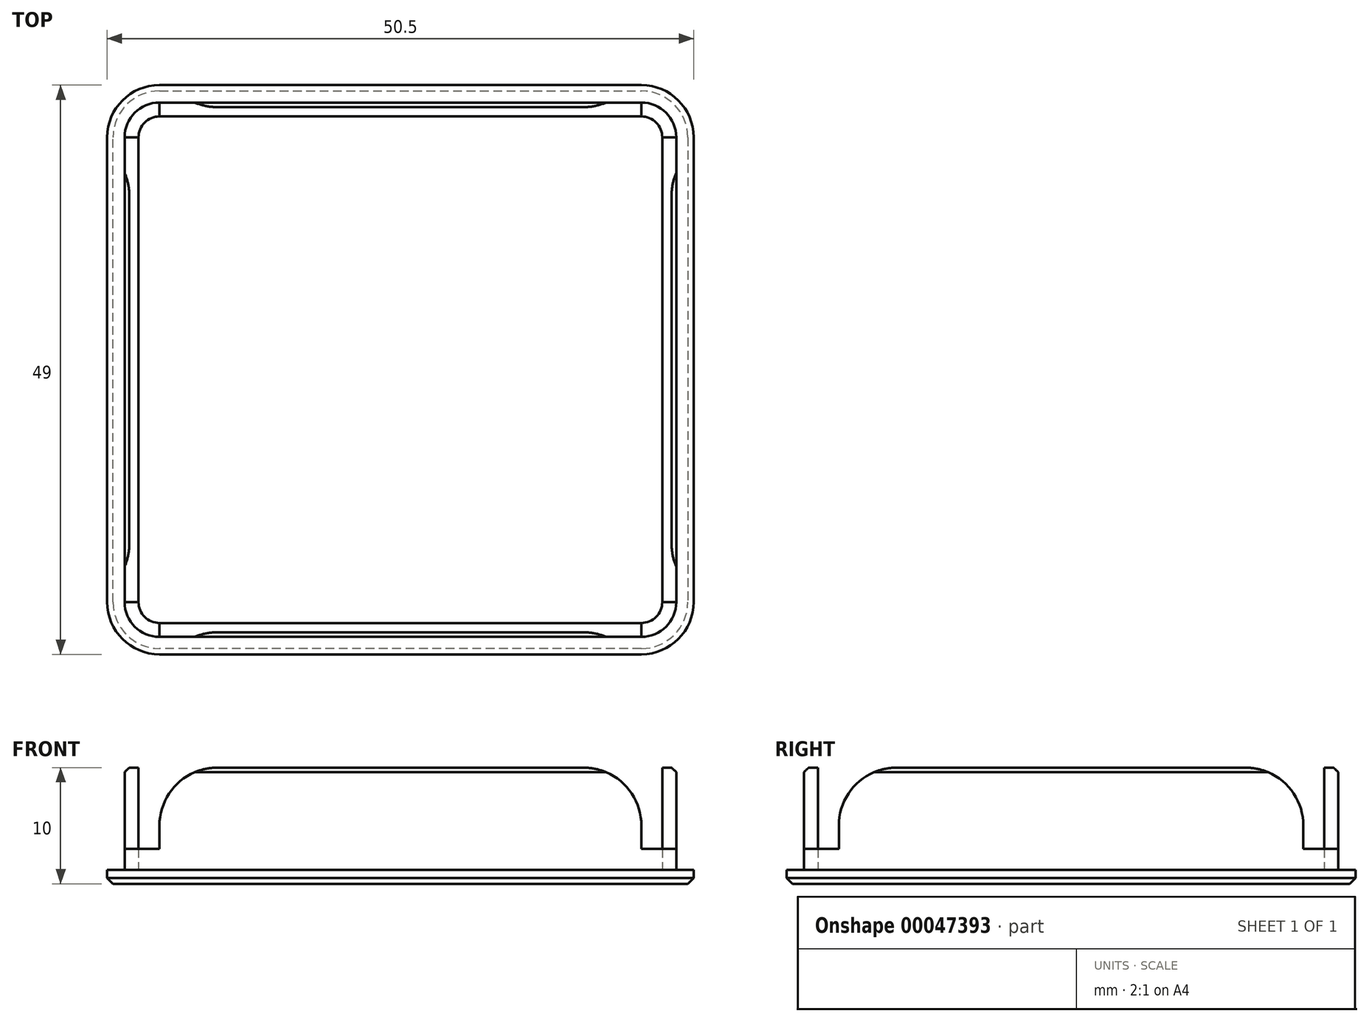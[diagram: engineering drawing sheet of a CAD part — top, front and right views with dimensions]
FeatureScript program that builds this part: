
annotation { "Feature Type Name" : "Feature", "Feature Type Description" : "" }
export const myFeature = defineFeature(function(context is Context, id is Id, definition is map)
    precondition{}
    {
        {
            var Q0;
            Q0=qCreatedBy(makeId("Top.planeOp"),FACE);
            var sketch = newSketch(context, id + "F0", { "sketchPlane" : qUnion([Q0])});
            skLineSegment(sketch, "E0.bottom", {"start": v(3, 0) * mm, "end": v(44.5, 0) * mm});
            skLineSegment(sketch, "E0.top", {"start": v(3, 46) * mm, "end": v(44.5, 46) * mm});
            skLineSegment(sketch, "E0.left", {"start": v(0, 3) * mm, "end": v(0, 43) * mm});
            skLineSegment(sketch, "E0.right", {"start": v(47.5, 3) * mm, "end": v(47.5, 43) * mm});
            skLineSegment(sketch, "E1.0", {"start": v(3, 47.5) * mm, "end": v(44.5, 47.5) * mm});
            skLineSegment(sketch, "E1.1", {"start": v(-1.5, 3) * mm, "end": v(-1.5, 43) * mm});
            skLineSegment(sketch, "E1.2", {"start": v(3, -1.5) * mm, "end": v(44.5, -1.5) * mm});
            skLineSegment(sketch, "E1.3", {"start": v(49, 3) * mm, "end": v(49, 43) * mm});
            skPoint(sketch, "E2.visualSharp", {"position": v(-1.5, 47.5) * mm});
            skArc(sketch, "E2.filletArc", {"start": v(3, 47.5) * mm, "mid": v(-0.18, 46.18) * mm, "end": v(-1.5, 43) * mm});
            skPoint(sketch, "E3.visualSharp", {"position": v(49, 47.5) * mm});
            skArc(sketch, "E3.filletArc", {"start": v(49, 43) * mm, "mid": v(47.68, 46.18) * mm, "end": v(44.5, 47.5) * mm});
            skPoint(sketch, "E4.visualSharp", {"position": v(49, -1.5) * mm});
            skArc(sketch, "E4.filletArc", {"start": v(44.5, -1.5) * mm, "mid": v(47.68, -0.18) * mm, "end": v(49, 3) * mm});
            skPoint(sketch, "E5.visualSharp", {"position": v(-1.5, -1.5) * mm});
            skArc(sketch, "E5.filletArc", {"start": v(-1.5, 3) * mm, "mid": v(-0.18, -0.18) * mm, "end": v(3, -1.5) * mm});
            skPoint(sketch, "E6.visualSharp", {"position": v(0, 46) * mm});
            skArc(sketch, "E6.filletArc", {"start": v(3, 46) * mm, "mid": v(0.88, 45.12) * mm, "end": v(0, 43) * mm});
            skPoint(sketch, "E7.visualSharp", {"position": v(47.5, 46) * mm});
            skArc(sketch, "E7.filletArc", {"start": v(47.5, 43) * mm, "mid": v(46.62, 45.12) * mm, "end": v(44.5, 46) * mm});
            skPoint(sketch, "E8.visualSharp", {"position": v(47.5, 0) * mm});
            skArc(sketch, "E8.filletArc", {"start": v(44.5, 0) * mm, "mid": v(46.62, 0.88) * mm, "end": v(47.5, 3) * mm});
            skPoint(sketch, "E9.visualSharp", {"position": v(0, 0) * mm});
            skArc(sketch, "E9.filletArc", {"start": v(0, 3) * mm, "mid": v(0.88, 0.88) * mm, "end": v(3, 0) * mm});
            skSolve(sketch);
        }
        {
            var Q0;
            Q0=makeQuery(id+"F0.imprint","IMPRINT",FACE,{"disambiguationData":[TD([[makeQuery(id+"F0.imprint","IMPRINT",EDGE,{"derivedFrom":sQuery(id+"F0.wireOp",EDGE,"E0.bottom")}),-1.0]])]});
            var Q1;
            Q1=makeQuery(id+"F0.imprint","IMPRINT",FACE,{"disambiguationData":[TD([[makeQuery(id+"F0.imprint","IMPRINT",EDGE,{"derivedFrom":sQuery(id+"F0.wireOp",EDGE,"E0.bottom")}),1.0]])]});
            extrude(context, id + "F1", {"entities" : qUnion([Q0, Q1]), "depth" : 1.2 * mm});
        }
        {
            var Q0;
            Q0=makeQuery(id+"F0.imprint","IMPRINT",FACE,{"disambiguationData":[TD([[makeQuery(id+"F0.imprint","IMPRINT",EDGE,{"derivedFrom":sQuery(id+"F0.wireOp",EDGE,"E0.bottom")}),1.0]])]});
            var sketch = newSketch(context, id + "F2", { "sketchPlane" : qUnion([Q0])});
            skLineSegment(sketch, "E10.0", {"start": v(1.2, 3) * mm, "end": v(1.2, 43) * mm});
            skLineSegment(sketch, "E10.1", {"start": v(3, 1.2) * mm, "end": v(44.5, 1.2) * mm});
            skLineSegment(sketch, "E10.2", {"start": v(46.3, 3) * mm, "end": v(46.3, 43) * mm});
            skLineSegment(sketch, "E10.3", {"start": v(3, 44.8) * mm, "end": v(44.5, 44.8) * mm});
            skPoint(sketch, "E11.visualSharp", {"position": v(1.2, 1.2) * mm});
            skArc(sketch, "E11.filletArc", {"start": v(1.2, 3) * mm, "mid": v(1.73, 1.73) * mm, "end": v(3, 1.2) * mm});
            skPoint(sketch, "E12.visualSharp", {"position": v(46.3, 1.2) * mm});
            skArc(sketch, "E12.filletArc", {"start": v(44.5, 1.2) * mm, "mid": v(45.77, 1.73) * mm, "end": v(46.3, 3) * mm});
            skPoint(sketch, "E13.visualSharp", {"position": v(46.3, 44.8) * mm});
            skArc(sketch, "E13.filletArc", {"start": v(46.3, 43) * mm, "mid": v(45.77, 44.27) * mm, "end": v(44.5, 44.8) * mm});
            skPoint(sketch, "E14.visualSharp", {"position": v(1.2, 44.8) * mm});
            skArc(sketch, "E14.filletArc", {"start": v(3, 44.8) * mm, "mid": v(1.73, 44.27) * mm, "end": v(1.2, 43) * mm});
            skLineSegment(sketch, "E15", {"start": v(3, 1.2) * mm, "end": v(3, 0) * mm});
            skLineSegment(sketch, "E16", {"start": v(44.5, 1.2) * mm, "end": v(44.5, 0) * mm});
            skLineSegment(sketch, "E17", {"start": v(46.3, 3) * mm, "end": v(47.5, 3) * mm});
            skLineSegment(sketch, "E18", {"start": v(46.3, 43) * mm, "end": v(47.5, 43) * mm});
            skLineSegment(sketch, "E19", {"start": v(1.2, 3) * mm, "end": v(0, 3) * mm});
            skLineSegment(sketch, "E20", {"start": v(1.2, 43) * mm, "end": v(0, 43) * mm});
            skLineSegment(sketch, "E21", {"start": v(3, 44.8) * mm, "end": v(3, 46) * mm});
            skLineSegment(sketch, "E22", {"start": v(44.5, 44.8) * mm, "end": v(44.5, 46) * mm});
            skSolve(sketch);
        }
        {
            var Q0;
            Q0=makeQuery(id+"F2.imprint","IMPRINT",FACE,{"disambiguationData":[TD([[makeQuery(id+"F2.imprint","IMPRINT",EDGE,{"derivedFrom":sQuery(id+"F2.wireOp",EDGE,"E10.0")}),1.0]])]});
            var Q1;
            Q1=makeQuery(id+"F2.imprint","IMPRINT",FACE,{"disambiguationData":[TD([[makeQuery(id+"F2.imprint","IMPRINT",EDGE,{"derivedFrom":sQuery(id+"F2.wireOp",EDGE,"E10.2")}),-1.0]])]});
            var Q2;
            Q2=makeQuery(id+"F2.imprint","IMPRINT",FACE,{"disambiguationData":[TD([[makeQuery(id+"F2.imprint","IMPRINT",EDGE,{"derivedFrom":sQuery(id+"F2.wireOp",EDGE,"E10.1")}),-1.0]])]});
            var Q3;
            Q3=makeQuery(id+"F2.imprint","IMPRINT",FACE,{"disambiguationData":[TD([[makeQuery(id+"F2.imprint","IMPRINT",EDGE,{"derivedFrom":sQuery(id+"F2.wireOp",EDGE,"E10.3")}),1.0]])]});
            extrude(context, id + "F3", {"entities" : qUnion([Q0, Q1, Q2, Q3]), "operationType" : NewBodyOperationType.ADD, "depth" : 10 * mm});
        }
        {
            var Q0;
            Q0=makeQuery(id+"F3.opExtrude","CAP_EDGE",EDGE,{"disambiguationData":[OSD([sQuery(id+"F0.wireOp",EDGE,"E0.right")])],"isStart":false});
            var Q1;
            Q1=makeQuery(id+"F3.opExtrude","CAP_EDGE",EDGE,{"disambiguationData":[OSD([sQuery(id+"F0.wireOp",EDGE,"E0.top")])],"isStart":false});
            var Q2;
            Q2=makeQuery(id+"F3.opExtrude","CAP_EDGE",EDGE,{"disambiguationData":[OSD([sQuery(id+"F0.wireOp",EDGE,"E0.left")])],"isStart":false});
            var Q3;
            Q3=makeQuery(id+"F3.opExtrude","CAP_EDGE",EDGE,{"disambiguationData":[OSD([sQuery(id+"F0.wireOp",EDGE,"E0.bottom")])],"isStart":false});
            chamfer(context, id + "F4", {"entities" : qUnion([Q0, Q1, Q2, Q3]), "width" : .4 * mm, "tangentPropagation" : true});
        }
        {
            var Q0;
            Q0=makeQuery(id+"F3.opExtrude","CAP_EDGE",EDGE,{"disambiguationData":[OSD([sQuery(id+"F2.wireOp",EDGE,"E18")])],"isStart":false});
            var Q1;
            Q1=makeQuery(id+"F3.opExtrude","CAP_EDGE",EDGE,{"disambiguationData":[OSD([sQuery(id+"F2.wireOp",EDGE,"E22")])],"isStart":false});
            var Q2;
            Q2=makeQuery(id+"F3.opExtrude","CAP_EDGE",EDGE,{"disambiguationData":[OSD([sQuery(id+"F2.wireOp",EDGE,"E21")])],"isStart":false});
            var Q3;
            Q3=makeQuery(id+"F3.opExtrude","CAP_EDGE",EDGE,{"disambiguationData":[OSD([sQuery(id+"F2.wireOp",EDGE,"E20")])],"isStart":false});
            var Q4;
            Q4=makeQuery(id+"F3.opExtrude","CAP_EDGE",EDGE,{"disambiguationData":[OSD([sQuery(id+"F2.wireOp",EDGE,"E15")])],"isStart":false});
            var Q5;
            Q5=makeQuery(id+"F3.opExtrude","CAP_EDGE",EDGE,{"disambiguationData":[OSD([sQuery(id+"F2.wireOp",EDGE,"E19")])],"isStart":false});
            var Q6;
            Q6=makeQuery(id+"F3.opExtrude","CAP_EDGE",EDGE,{"disambiguationData":[OSD([sQuery(id+"F2.wireOp",EDGE,"E17")])],"isStart":false});
            var Q7;
            Q7=makeQuery(id+"F3.opExtrude","CAP_EDGE",EDGE,{"disambiguationData":[OSD([sQuery(id+"F2.wireOp",EDGE,"E16")])],"isStart":false});
            fillet(context, id + "F5", {"entities" : qUnion([Q0, Q1, Q2, Q3, Q4, Q5, Q6, Q7]), "radius" : 5 * mm, "tangentPropagation" : true, "allowEdgeOverflow" : false});
        }
        {
            var Q0;
            Q0=makeQuery(id+"F2.imprint","IMPRINT",FACE,{"disambiguationData":[TD([[makeQuery(id+"F2.imprint","IMPRINT",EDGE,{"derivedFrom":sQuery(id+"F2.wireOp",EDGE,"E14.filletArc")}),-1.0]])]});
            var Q1;
            Q1=makeQuery(id+"F2.imprint","IMPRINT",FACE,{"disambiguationData":[TD([[makeQuery(id+"F2.imprint","IMPRINT",EDGE,{"derivedFrom":sQuery(id+"F2.wireOp",EDGE,"E11.filletArc")}),-1.0]])]});
            var Q2;
            Q2=makeQuery(id+"F2.imprint","IMPRINT",FACE,{"disambiguationData":[TD([[makeQuery(id+"F2.imprint","IMPRINT",EDGE,{"derivedFrom":sQuery(id+"F2.wireOp",EDGE,"E12.filletArc")}),-1.0]])]});
            var Q3;
            Q3=makeQuery(id+"F2.imprint","IMPRINT",FACE,{"disambiguationData":[TD([[makeQuery(id+"F2.imprint","IMPRINT",EDGE,{"derivedFrom":sQuery(id+"F2.wireOp",EDGE,"E13.filletArc")}),-1.0]])]});
            extrude(context, id + "F6", {"entities" : qUnion([Q0, Q1, Q2, Q3]), "operationType" : NewBodyOperationType.ADD, "depth" : 3 * mm});
        }
        {
            var Q0;
            Q0=makeQuery(id+"F1.opExtrude","CAP_FACE",FACE,{"disambiguationData":[OSD([sQuery(id+"F0.wireOp",EDGE,"E1.0"),sQuery(id+"F0.wireOp",EDGE,"E1.1"),sQuery(id+"F0.wireOp",EDGE,"E1.2"),sQuery(id+"F0.wireOp",EDGE,"E1.3"),sQuery(id+"F0.wireOp",EDGE,"E2.filletArc"),sQuery(id+"F0.wireOp",EDGE,"E3.filletArc"),sQuery(id+"F0.wireOp",EDGE,"E4.filletArc"),sQuery(id+"F0.wireOp",EDGE,"E5.filletArc")])],"isStart":true});
            chamfer(context, id + "F7", {"entities" : qUnion([Q0]), "width" : .5 * mm, "tangentPropagation" : true});
        }
    });
